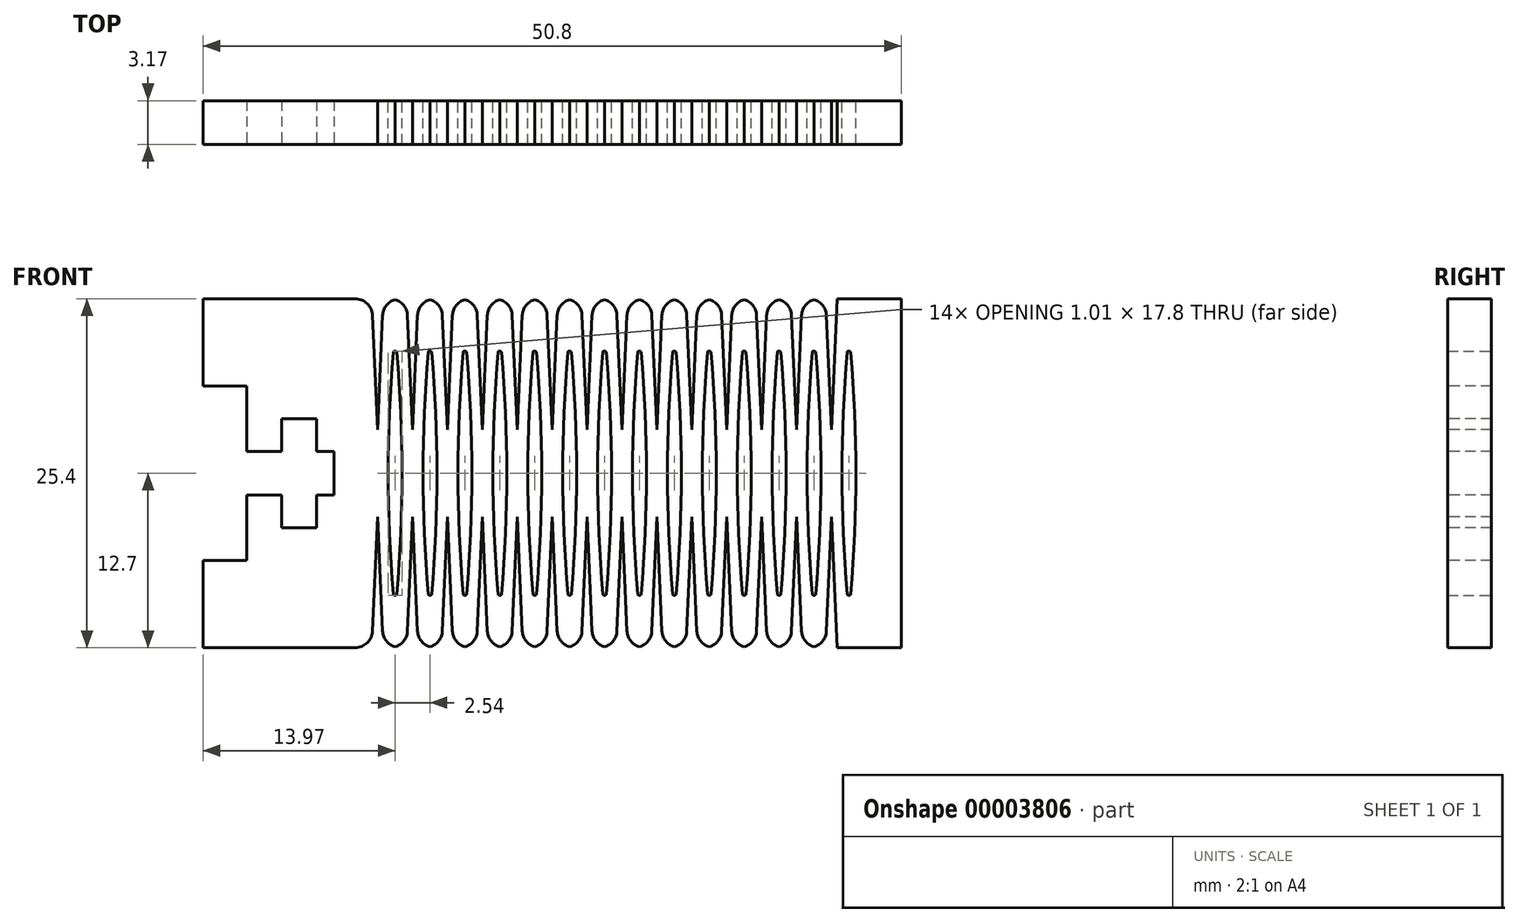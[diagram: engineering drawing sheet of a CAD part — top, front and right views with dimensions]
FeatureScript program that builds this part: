
annotation { "Feature Type Name" : "Feature", "Feature Type Description" : "" }
export const myFeature = defineFeature(function(context is Context, id is Id, definition is map)
    precondition{}
    {
        {
            var Q0;
            Q0=qCreatedBy(makeId("Front.planeOp"),FACE);
            var sketch = newSketch(context, id + "F0", { "sketchPlane" : qUnion([Q0])});
            skLineSegment(sketch, "E0.bottom", {"start": v(0, 0) * mm, "end": v(50.8, 0) * mm});
            skLineSegment(sketch, "E0.top", {"start": v(0, 25.4) * mm, "end": v(50.8, 25.4) * mm});
            skLineSegment(sketch, "E0.left", {"start": v(0, 0) * mm, "end": v(0, 25.4) * mm});
            skLineSegment(sketch, "E0.right", {"start": v(50.8, 0) * mm, "end": v(50.8, 25.4) * mm});
            skSolve(sketch);
        }
        {
            var Q0;
            Q0 = qSketchRegion(id + "F0", true);
            extrude(context, id + "F1", {"entities" : qUnion([Q0]), "oppositeDirection" : true, "depth" : 3.17 * mm});
        }
        {
            var Q0;
            Q0=makeQuery(id+"F1.opExtrude","CAP_FACE",FACE,{"disambiguationData":[OSD([sQuery(id+"F0.wireOp",EDGE,"E0.bottom"),sQuery(id+"F0.wireOp",EDGE,"E0.top"),sQuery(id+"F0.wireOp",EDGE,"E0.left"),sQuery(id+"F0.wireOp",EDGE,"E0.right")])],"isStart":true});
            var sketch = newSketch(context, id + "F2", { "sketchPlane" : qUnion([Q0])});
            skLineSegment(sketch, "E1.bottom", {"start": v(0, 6.35) * mm, "end": v(3.18, 6.35) * mm});
            skLineSegment(sketch, "E1.top", {"start": v(0, 19.05) * mm, "end": v(3.17, 19.05) * mm});
            skLineSegment(sketch, "E1.left", {"start": v(0, 6.35) * mm, "end": v(0, 19.05) * mm});
            skLineSegment(sketch, "E1.right", {"start": v(3.18, 6.35) * mm, "end": v(3.18, 19.05) * mm});
            skLineSegment(sketch, "E2.bottom", {"start": v(0, 11.11) * mm, "end": v(9.53, 11.11) * mm});
            skLineSegment(sketch, "E2.top", {"start": v(0, 14.29) * mm, "end": v(9.53, 14.29) * mm});
            skLineSegment(sketch, "E2.left", {"start": v(0, 11.11) * mm, "end": v(0, 14.29) * mm});
            skLineSegment(sketch, "E2.right", {"start": v(9.53, 11.11) * mm, "end": v(9.53, 14.29) * mm});
            skLineSegment(sketch, "E3.bottom", {"start": v(5.71, 16.67) * mm, "end": v(8.26, 16.67) * mm});
            skLineSegment(sketch, "E3.top", {"start": v(5.71, 8.73) * mm, "end": v(8.26, 8.73) * mm});
            skLineSegment(sketch, "E3.left", {"start": v(5.71, 16.67) * mm, "end": v(5.71, 8.73) * mm});
            skLineSegment(sketch, "E3.right", {"start": v(8.26, 16.67) * mm, "end": v(8.26, 8.73) * mm});
            skSolve(sketch);
        }
        {
            var Q0;
            Q0 = qSketchRegion(id + "F2", true);
            extrude(context, id + "F3", {"entities" : qUnion([Q0]), "operationType" : NewBodyOperationType.REMOVE, "endBound" : BoundingType.THROUGH_ALL, "oppositeDirection" : true, "depth" : 25.4 * mm});
        }
        {
            var Q0;
            Q0=makeQuery(id+"F1.opExtrude","CAP_FACE",FACE,{"disambiguationData":[OSD([sQuery(id+"F0.wireOp",EDGE,"E0.bottom"),sQuery(id+"F0.wireOp",EDGE,"E0.top"),sQuery(id+"F0.wireOp",EDGE,"E0.left"),sQuery(id+"F0.wireOp",EDGE,"E0.right")])],"isStart":true});
            var sketch = newSketch(context, id + "F4", { "sketchPlane" : qUnion([Q0])});
            skLineSegment(sketch, "E4", {"start": v(0, 9.53) * mm, "end": v(50.8, 9.53) * mm, "construction": true});
            skLineSegment(sketch, "E5", {"start": v(12.7, 9.53) * mm, "end": v(12.28, 0) * mm});
            skLineSegment(sketch, "E6", {"start": v(12.7, 9.53) * mm, "end": v(13.12, 0) * mm});
            skLineSegment(sketch, "E7", {"start": v(12.28, 0) * mm, "end": v(13.12, 0) * mm});
            skLineSegment(sketch, "E8", {"start": v(12.7, 0) * mm, "end": v(12.7, 9.53) * mm, "construction": true});
            skLineSegment(sketch, "E9", {"start": v(0, 12.7) * mm, "end": v(50.8, 12.7) * mm, "construction": true});
            skLineSegment(sketch, "E10.0.MirrorCS", {"start": v(12.7, 15.87) * mm, "end": v(13.12, 25.4) * mm});
            skLineSegment(sketch, "E11.0.MirrorCS", {"start": v(12.7, 15.88) * mm, "end": v(12.28, 25.4) * mm});
            skLineSegment(sketch, "E12.0.MirrorCS", {"start": v(12.28, 25.4) * mm, "end": v(13.12, 25.4) * mm});
            skLineSegment(sketch, "E13.1.0.0", {"start": v(15.24, 9.53) * mm, "end": v(15.66, 0) * mm});
            skLineSegment(sketch, "E13.1.0.1", {"start": v(15.24, 9.52) * mm, "end": v(14.82, 0) * mm});
            skLineSegment(sketch, "E13.1.0.2", {"start": v(14.82, 0) * mm, "end": v(15.66, 0) * mm});
            skLineSegment(sketch, "E13.2.0.0", {"start": v(17.78, 9.53) * mm, "end": v(18.2, 0) * mm});
            skLineSegment(sketch, "E13.2.0.1", {"start": v(17.78, 9.52) * mm, "end": v(17.36, 0) * mm});
            skLineSegment(sketch, "E13.2.0.2", {"start": v(17.36, 0) * mm, "end": v(18.2, 0) * mm});
            skLineSegment(sketch, "E13.3.0.0", {"start": v(20.32, 9.53) * mm, "end": v(20.74, 0) * mm});
            skLineSegment(sketch, "E13.3.0.1", {"start": v(20.32, 9.52) * mm, "end": v(19.9, 0) * mm});
            skLineSegment(sketch, "E13.3.0.2", {"start": v(19.9, 0) * mm, "end": v(20.74, 0) * mm});
            skLineSegment(sketch, "E13.4.0.0", {"start": v(22.86, 9.53) * mm, "end": v(23.28, 0) * mm});
            skLineSegment(sketch, "E13.4.0.1", {"start": v(22.86, 9.53) * mm, "end": v(22.44, 0) * mm});
            skLineSegment(sketch, "E13.4.0.2", {"start": v(22.44, 0) * mm, "end": v(23.28, 0) * mm});
            skLineSegment(sketch, "E13.5.0.0", {"start": v(25.4, 9.53) * mm, "end": v(25.82, 0) * mm});
            skLineSegment(sketch, "E13.5.0.1", {"start": v(25.4, 9.52) * mm, "end": v(24.98, 0) * mm});
            skLineSegment(sketch, "E13.5.0.2", {"start": v(24.98, 0) * mm, "end": v(25.82, 0) * mm});
            skLineSegment(sketch, "E13.6.0.0", {"start": v(27.94, 9.53) * mm, "end": v(28.36, 0) * mm});
            skLineSegment(sketch, "E13.6.0.1", {"start": v(27.94, 9.52) * mm, "end": v(27.52, 0) * mm});
            skLineSegment(sketch, "E13.6.0.2", {"start": v(27.52, 0) * mm, "end": v(28.36, 0) * mm});
            skLineSegment(sketch, "E13.7.0.0", {"start": v(30.48, 9.53) * mm, "end": v(30.9, 0) * mm});
            skLineSegment(sketch, "E13.7.0.1", {"start": v(30.48, 9.52) * mm, "end": v(30.06, 0) * mm});
            skLineSegment(sketch, "E13.7.0.2", {"start": v(30.06, 0) * mm, "end": v(30.9, 0) * mm});
            skLineSegment(sketch, "E13.8.0.0", {"start": v(33.02, 9.53) * mm, "end": v(33.44, 0) * mm});
            skLineSegment(sketch, "E13.8.0.1", {"start": v(33.02, 9.52) * mm, "end": v(32.6, 0) * mm});
            skLineSegment(sketch, "E13.8.0.2", {"start": v(32.6, 0) * mm, "end": v(33.44, 0) * mm});
            skLineSegment(sketch, "E13.9.0.0", {"start": v(35.56, 9.53) * mm, "end": v(35.98, 0) * mm});
            skLineSegment(sketch, "E13.9.0.1", {"start": v(35.56, 9.53) * mm, "end": v(35.14, 0) * mm});
            skLineSegment(sketch, "E13.9.0.2", {"start": v(35.14, 0) * mm, "end": v(35.98, 0) * mm});
            skLineSegment(sketch, "E13.10.0.0", {"start": v(38.1, 9.53) * mm, "end": v(38.52, 0) * mm});
            skLineSegment(sketch, "E13.10.0.1", {"start": v(38.1, 9.53) * mm, "end": v(37.68, 0) * mm});
            skLineSegment(sketch, "E13.10.0.2", {"start": v(37.68, 0) * mm, "end": v(38.52, 0) * mm});
            skLineSegment(sketch, "E13.11.0.0", {"start": v(40.64, 9.53) * mm, "end": v(41.06, 0) * mm});
            skLineSegment(sketch, "E13.11.0.1", {"start": v(40.64, 9.52) * mm, "end": v(40.22, 0) * mm});
            skLineSegment(sketch, "E13.11.0.2", {"start": v(40.22, 0) * mm, "end": v(41.06, 0) * mm});
            skLineSegment(sketch, "E13.12.0.0", {"start": v(43.18, 9.53) * mm, "end": v(43.6, 0) * mm});
            skLineSegment(sketch, "E13.12.0.1", {"start": v(43.18, 9.52) * mm, "end": v(42.76, 0) * mm});
            skLineSegment(sketch, "E13.12.0.2", {"start": v(42.76, 0) * mm, "end": v(43.6, 0) * mm});
            skLineSegment(sketch, "E13.13.0.0", {"start": v(45.72, 9.53) * mm, "end": v(46.14, 0) * mm});
            skLineSegment(sketch, "E13.13.0.1", {"start": v(45.72, 9.52) * mm, "end": v(45.3, 0) * mm});
            skLineSegment(sketch, "E13.13.0.2", {"start": v(45.3, 0) * mm, "end": v(46.14, 0) * mm});
            skLineSegment(sketch, "E13.direction1", {"start": v(13.12, 0) * mm, "end": v(15.66, 0) * mm, "construction": true});
            skLineSegment(sketch, "E14.1.MirrorCS", {"start": v(30.06, 25.4) * mm, "end": v(30.9, 25.4) * mm});
            skLineSegment(sketch, "E14.2.MirrorCS", {"start": v(14.82, 25.4) * mm, "end": v(15.66, 25.4) * mm});
            skLineSegment(sketch, "E14.4.MirrorCS", {"start": v(22.44, 25.4) * mm, "end": v(23.28, 25.4) * mm});
            skLineSegment(sketch, "E14.5.MirrorCS", {"start": v(42.76, 25.4) * mm, "end": v(43.6, 25.4) * mm});
            skLineSegment(sketch, "E14.6.MirrorCS", {"start": v(40.22, 25.4) * mm, "end": v(41.06, 25.4) * mm});
            skLineSegment(sketch, "E14.8.MirrorCS", {"start": v(27.52, 25.4) * mm, "end": v(28.36, 25.4) * mm});
            skLineSegment(sketch, "E14.9.MirrorCS", {"start": v(35.14, 25.4) * mm, "end": v(35.98, 25.4) * mm});
            skLineSegment(sketch, "E14.10.MirrorCS", {"start": v(32.6, 25.4) * mm, "end": v(33.44, 25.4) * mm});
            skLineSegment(sketch, "E14.11.MirrorCS", {"start": v(24.98, 25.4) * mm, "end": v(25.82, 25.4) * mm});
            skLineSegment(sketch, "E14.13.MirrorCS", {"start": v(19.9, 25.4) * mm, "end": v(20.74, 25.4) * mm});
            skLineSegment(sketch, "E14.14.MirrorCS", {"start": v(37.68, 25.4) * mm, "end": v(38.52, 25.4) * mm});
            skLineSegment(sketch, "E14.15.MirrorCS", {"start": v(45.3, 25.4) * mm, "end": v(46.14, 25.4) * mm});
            skLineSegment(sketch, "E14.16.MirrorCS", {"start": v(17.36, 25.4) * mm, "end": v(18.2, 25.4) * mm});
            skLineSegment(sketch, "E14.17.MirrorCS", {"start": v(43.18, 15.88) * mm, "end": v(42.76, 25.4) * mm});
            skLineSegment(sketch, "E14.18.MirrorCS", {"start": v(30.48, 15.88) * mm, "end": v(30.9, 25.4) * mm});
            skLineSegment(sketch, "E14.19.MirrorCS", {"start": v(38.1, 15.88) * mm, "end": v(38.52, 25.4) * mm});
            skLineSegment(sketch, "E14.21.MirrorCS", {"start": v(30.48, 15.88) * mm, "end": v(30.06, 25.4) * mm});
            skLineSegment(sketch, "E14.22.MirrorCS", {"start": v(38.1, 15.88) * mm, "end": v(37.68, 25.4) * mm});
            skLineSegment(sketch, "E14.23.MirrorCS", {"start": v(25.4, 15.88) * mm, "end": v(25.82, 25.4) * mm});
            skLineSegment(sketch, "E14.24.MirrorCS", {"start": v(27.94, 15.88) * mm, "end": v(27.52, 25.4) * mm});
            skLineSegment(sketch, "E14.26.MirrorCS", {"start": v(35.56, 15.88) * mm, "end": v(35.14, 25.4) * mm});
            skLineSegment(sketch, "E14.27.MirrorCS", {"start": v(22.86, 15.88) * mm, "end": v(23.28, 25.4) * mm});
            skLineSegment(sketch, "E14.28.MirrorCS", {"start": v(43.18, 15.88) * mm, "end": v(43.6, 25.4) * mm});
            skLineSegment(sketch, "E14.30.MirrorCS", {"start": v(22.86, 15.88) * mm, "end": v(22.44, 25.4) * mm});
            skLineSegment(sketch, "E14.33.MirrorCS", {"start": v(20.32, 15.88) * mm, "end": v(19.9, 25.4) * mm});
            skLineSegment(sketch, "E14.34.MirrorCS", {"start": v(40.64, 15.88) * mm, "end": v(41.06, 25.4) * mm});
            skLineSegment(sketch, "E14.36.MirrorCS", {"start": v(27.94, 15.88) * mm, "end": v(28.36, 25.4) * mm});
            skLineSegment(sketch, "E14.37.MirrorCS", {"start": v(40.64, 15.88) * mm, "end": v(40.22, 25.4) * mm});
            skLineSegment(sketch, "E14.39.MirrorCS", {"start": v(35.56, 15.88) * mm, "end": v(35.98, 25.4) * mm});
            skLineSegment(sketch, "E14.41.MirrorCS", {"start": v(25.4, 15.88) * mm, "end": v(24.98, 25.4) * mm});
            skLineSegment(sketch, "E14.42.MirrorCS", {"start": v(33.02, 15.88) * mm, "end": v(32.6, 25.4) * mm});
            skLineSegment(sketch, "E14.43.MirrorCS", {"start": v(17.78, 15.88) * mm, "end": v(17.36, 25.4) * mm});
            skLineSegment(sketch, "E14.44.MirrorCS", {"start": v(45.72, 15.88) * mm, "end": v(46.14, 25.4) * mm});
            skLineSegment(sketch, "E14.45.MirrorCS", {"start": v(20.32, 15.88) * mm, "end": v(20.74, 25.4) * mm});
            skLineSegment(sketch, "E14.46.MirrorCS", {"start": v(45.72, 15.88) * mm, "end": v(45.3, 25.4) * mm});
            skLineSegment(sketch, "E14.47.MirrorCS", {"start": v(15.24, 15.88) * mm, "end": v(15.66, 25.4) * mm});
            skLineSegment(sketch, "E14.48.MirrorCS", {"start": v(33.02, 15.88) * mm, "end": v(33.44, 25.4) * mm});
            skLineSegment(sketch, "E14.49.MirrorCS", {"start": v(15.24, 15.88) * mm, "end": v(14.82, 25.4) * mm});
            skLineSegment(sketch, "E14.50.MirrorCS", {"start": v(17.78, 15.88) * mm, "end": v(18.2, 25.4) * mm});
            skLineSegment(sketch, "E15", {"start": v(13.97, 22.86) * mm, "end": v(13.97, 2.54) * mm, "construction": true});
            skLineSegment(sketch, "E16", {"start": v(13.02, 12.7) * mm, "end": v(14.92, 12.7) * mm, "construction": true});
            skLineSegment(sketch, "E17", {"start": v(13.97, 22.86) * mm, "end": v(13.02, 12.7) * mm});
            skLineSegment(sketch, "E18", {"start": v(13.97, 2.54) * mm, "end": v(14.92, 12.7) * mm});
            skLineSegment(sketch, "E19", {"start": v(14.92, 12.7) * mm, "end": v(13.97, 22.86) * mm});
            skLineSegment(sketch, "E20", {"start": v(13.02, 12.7) * mm, "end": v(13.97, 2.54) * mm});
            skLineSegment(sketch, "E21.1.0.0", {"start": v(16.51, 22.86) * mm, "end": v(15.56, 12.7) * mm});
            skLineSegment(sketch, "E21.1.0.1", {"start": v(17.46, 12.7) * mm, "end": v(16.51, 22.86) * mm});
            skLineSegment(sketch, "E21.1.0.2", {"start": v(15.56, 12.7) * mm, "end": v(16.51, 2.54) * mm});
            skLineSegment(sketch, "E21.1.0.3", {"start": v(16.51, 2.54) * mm, "end": v(17.46, 12.7) * mm});
            skLineSegment(sketch, "E21.2.0.0", {"start": v(19.05, 22.86) * mm, "end": v(18.1, 12.7) * mm});
            skLineSegment(sketch, "E21.2.0.1", {"start": v(20, 12.7) * mm, "end": v(19.05, 22.86) * mm});
            skLineSegment(sketch, "E21.2.0.2", {"start": v(18.1, 12.7) * mm, "end": v(19.05, 2.54) * mm});
            skLineSegment(sketch, "E21.2.0.3", {"start": v(19.05, 2.54) * mm, "end": v(20, 12.7) * mm});
            skLineSegment(sketch, "E21.3.0.0", {"start": v(21.6, 22.86) * mm, "end": v(20.64, 12.7) * mm});
            skLineSegment(sketch, "E21.3.0.1", {"start": v(22.54, 12.7) * mm, "end": v(21.59, 22.86) * mm});
            skLineSegment(sketch, "E21.3.0.2", {"start": v(20.64, 12.7) * mm, "end": v(21.6, 2.54) * mm});
            skLineSegment(sketch, "E21.3.0.3", {"start": v(21.6, 2.54) * mm, "end": v(22.54, 12.7) * mm});
            skLineSegment(sketch, "E21.4.0.0", {"start": v(24.13, 22.86) * mm, "end": v(23.18, 12.7) * mm});
            skLineSegment(sketch, "E21.4.0.1", {"start": v(25.08, 12.7) * mm, "end": v(24.13, 22.86) * mm});
            skLineSegment(sketch, "E21.4.0.2", {"start": v(23.18, 12.7) * mm, "end": v(24.13, 2.54) * mm});
            skLineSegment(sketch, "E21.4.0.3", {"start": v(24.13, 2.54) * mm, "end": v(25.08, 12.7) * mm});
            skLineSegment(sketch, "E21.5.0.0", {"start": v(26.67, 22.86) * mm, "end": v(25.72, 12.7) * mm});
            skLineSegment(sketch, "E21.5.0.1", {"start": v(27.62, 12.7) * mm, "end": v(26.67, 22.86) * mm});
            skLineSegment(sketch, "E21.5.0.2", {"start": v(25.72, 12.7) * mm, "end": v(26.67, 2.54) * mm});
            skLineSegment(sketch, "E21.5.0.3", {"start": v(26.67, 2.54) * mm, "end": v(27.62, 12.7) * mm});
            skLineSegment(sketch, "E21.6.0.0", {"start": v(29.21, 22.86) * mm, "end": v(28.26, 12.7) * mm});
            skLineSegment(sketch, "E21.6.0.1", {"start": v(30.16, 12.7) * mm, "end": v(29.21, 22.86) * mm});
            skLineSegment(sketch, "E21.6.0.2", {"start": v(28.26, 12.7) * mm, "end": v(29.21, 2.54) * mm});
            skLineSegment(sketch, "E21.6.0.3", {"start": v(29.21, 2.54) * mm, "end": v(30.16, 12.7) * mm});
            skLineSegment(sketch, "E21.7.0.0", {"start": v(31.75, 22.86) * mm, "end": v(30.8, 12.7) * mm});
            skLineSegment(sketch, "E21.7.0.1", {"start": v(32.7, 12.7) * mm, "end": v(31.75, 22.86) * mm});
            skLineSegment(sketch, "E21.7.0.2", {"start": v(30.8, 12.7) * mm, "end": v(31.75, 2.54) * mm});
            skLineSegment(sketch, "E21.7.0.3", {"start": v(31.75, 2.54) * mm, "end": v(32.7, 12.7) * mm});
            skLineSegment(sketch, "E21.8.0.0", {"start": v(34.3, 22.86) * mm, "end": v(33.34, 12.7) * mm});
            skLineSegment(sketch, "E21.8.0.1", {"start": v(35.24, 12.7) * mm, "end": v(34.3, 22.86) * mm});
            skLineSegment(sketch, "E21.8.0.2", {"start": v(33.34, 12.7) * mm, "end": v(34.3, 2.54) * mm});
            skLineSegment(sketch, "E21.8.0.3", {"start": v(34.3, 2.54) * mm, "end": v(35.24, 12.7) * mm});
            skLineSegment(sketch, "E21.9.0.0", {"start": v(36.83, 22.86) * mm, "end": v(35.88, 12.7) * mm});
            skLineSegment(sketch, "E21.9.0.1", {"start": v(37.78, 12.7) * mm, "end": v(36.83, 22.86) * mm});
            skLineSegment(sketch, "E21.9.0.2", {"start": v(35.88, 12.7) * mm, "end": v(36.83, 2.54) * mm});
            skLineSegment(sketch, "E21.9.0.3", {"start": v(36.83, 2.54) * mm, "end": v(37.78, 12.7) * mm});
            skLineSegment(sketch, "E21.10.0.0", {"start": v(39.37, 22.86) * mm, "end": v(38.42, 12.7) * mm});
            skLineSegment(sketch, "E21.10.0.1", {"start": v(40.32, 12.7) * mm, "end": v(39.37, 22.86) * mm});
            skLineSegment(sketch, "E21.10.0.2", {"start": v(38.42, 12.7) * mm, "end": v(39.37, 2.54) * mm});
            skLineSegment(sketch, "E21.10.0.3", {"start": v(39.37, 2.54) * mm, "end": v(40.32, 12.7) * mm});
            skLineSegment(sketch, "E21.11.0.0", {"start": v(41.91, 22.86) * mm, "end": v(40.96, 12.7) * mm});
            skLineSegment(sketch, "E21.11.0.1", {"start": v(42.86, 12.7) * mm, "end": v(41.91, 22.86) * mm});
            skLineSegment(sketch, "E21.11.0.2", {"start": v(40.96, 12.7) * mm, "end": v(41.91, 2.54) * mm});
            skLineSegment(sketch, "E21.11.0.3", {"start": v(41.91, 2.54) * mm, "end": v(42.86, 12.7) * mm});
            skLineSegment(sketch, "E21.12.0.0", {"start": v(44.45, 22.86) * mm, "end": v(43.5, 12.7) * mm});
            skLineSegment(sketch, "E21.12.0.1", {"start": v(45.4, 12.7) * mm, "end": v(44.45, 22.86) * mm});
            skLineSegment(sketch, "E21.12.0.2", {"start": v(43.5, 12.7) * mm, "end": v(44.45, 2.54) * mm});
            skLineSegment(sketch, "E21.12.0.3", {"start": v(44.45, 2.54) * mm, "end": v(45.4, 12.7) * mm});
            skLineSegment(sketch, "E21.13.0.0", {"start": v(47, 22.86) * mm, "end": v(46.04, 12.7) * mm});
            skLineSegment(sketch, "E21.13.0.1", {"start": v(47.94, 12.7) * mm, "end": v(47, 22.86) * mm});
            skLineSegment(sketch, "E21.13.0.2", {"start": v(46.04, 12.7) * mm, "end": v(47, 2.54) * mm});
            skLineSegment(sketch, "E21.13.0.3", {"start": v(47, 2.54) * mm, "end": v(47.94, 12.7) * mm});
            skLineSegment(sketch, "E21.direction1", {"start": v(13.02, 12.7) * mm, "end": v(15.56, 12.7) * mm, "construction": true});
            skSolve(sketch);
        }
        {
            var Q0;
            Q0 = qSketchRegion(id + "F4", true);
            extrude(context, id + "F5", {"entities" : qUnion([Q0]), "operationType" : NewBodyOperationType.REMOVE, "endBound" : BoundingType.THROUGH_ALL, "oppositeDirection" : true, "depth" : 25.4 * mm});
        }
        {
            var Q0;
            Q0=makeQuery(id+"F5.boolean.opBoolean","COPY",EDGE,{"derivedFrom":makeQuery(id+"F5.opExtrude","SWEPT_EDGE",EDGE,{"disambiguationData":[OSD([sQuery(id+"F4.wireOp",EDGE,"E17"),sQuery(id+"F4.wireOp",EDGE,"E20")])]})});
            var Q1;
            Q1=makeQuery(id+"F5.boolean.opBoolean","COPY",EDGE,{"derivedFrom":makeQuery(id+"F5.opExtrude","SWEPT_EDGE",EDGE,{"disambiguationData":[OSD([sQuery(id+"F4.wireOp",EDGE,"E21.1.0.0"),sQuery(id+"F4.wireOp",EDGE,"E21.1.0.2")])]})});
            var Q2;
            Q2=makeQuery(id+"F5.boolean.opBoolean","COPY",EDGE,{"derivedFrom":makeQuery(id+"F5.opExtrude","SWEPT_EDGE",EDGE,{"disambiguationData":[OSD([sQuery(id+"F4.wireOp",EDGE,"E21.2.0.0"),sQuery(id+"F4.wireOp",EDGE,"E21.2.0.2")])]})});
            var Q3;
            Q3=makeQuery(id+"F5.boolean.opBoolean","COPY",EDGE,{"derivedFrom":makeQuery(id+"F5.opExtrude","SWEPT_EDGE",EDGE,{"disambiguationData":[OSD([sQuery(id+"F4.wireOp",EDGE,"E21.3.0.0"),sQuery(id+"F4.wireOp",EDGE,"E21.3.0.2")])]})});
            var Q4;
            Q4=makeQuery(id+"F5.boolean.opBoolean","COPY",EDGE,{"derivedFrom":makeQuery(id+"F5.opExtrude","SWEPT_EDGE",EDGE,{"disambiguationData":[OSD([sQuery(id+"F4.wireOp",EDGE,"E21.4.0.0"),sQuery(id+"F4.wireOp",EDGE,"E21.4.0.2")])]})});
            var Q5;
            Q5=makeQuery(id+"F5.boolean.opBoolean","COPY",EDGE,{"derivedFrom":makeQuery(id+"F5.opExtrude","SWEPT_EDGE",EDGE,{"disambiguationData":[OSD([sQuery(id+"F4.wireOp",EDGE,"E21.5.0.0"),sQuery(id+"F4.wireOp",EDGE,"E21.5.0.2")])]})});
            var Q6;
            Q6=makeQuery(id+"F5.boolean.opBoolean","COPY",EDGE,{"derivedFrom":makeQuery(id+"F5.opExtrude","SWEPT_EDGE",EDGE,{"disambiguationData":[OSD([sQuery(id+"F4.wireOp",EDGE,"E21.6.0.0"),sQuery(id+"F4.wireOp",EDGE,"E21.6.0.2")])]})});
            var Q7;
            Q7=makeQuery(id+"F5.boolean.opBoolean","COPY",EDGE,{"derivedFrom":makeQuery(id+"F5.opExtrude","SWEPT_EDGE",EDGE,{"disambiguationData":[OSD([sQuery(id+"F4.wireOp",EDGE,"E21.7.0.0"),sQuery(id+"F4.wireOp",EDGE,"E21.7.0.2")])]})});
            var Q8;
            Q8=makeQuery(id+"F5.boolean.opBoolean","COPY",EDGE,{"derivedFrom":makeQuery(id+"F5.opExtrude","SWEPT_EDGE",EDGE,{"disambiguationData":[OSD([sQuery(id+"F4.wireOp",EDGE,"E21.8.0.0"),sQuery(id+"F4.wireOp",EDGE,"E21.8.0.2")])]})});
            var Q9;
            Q9=makeQuery(id+"F5.boolean.opBoolean","COPY",EDGE,{"derivedFrom":makeQuery(id+"F5.opExtrude","SWEPT_EDGE",EDGE,{"disambiguationData":[OSD([sQuery(id+"F4.wireOp",EDGE,"E21.9.0.0"),sQuery(id+"F4.wireOp",EDGE,"E21.9.0.2")])]})});
            var Q10;
            Q10=makeQuery(id+"F5.boolean.opBoolean","COPY",EDGE,{"derivedFrom":makeQuery(id+"F5.opExtrude","SWEPT_EDGE",EDGE,{"disambiguationData":[OSD([sQuery(id+"F4.wireOp",EDGE,"E21.10.0.0"),sQuery(id+"F4.wireOp",EDGE,"E21.10.0.2")])]})});
            var Q11;
            Q11=makeQuery(id+"F5.boolean.opBoolean","COPY",EDGE,{"derivedFrom":makeQuery(id+"F5.opExtrude","SWEPT_EDGE",EDGE,{"disambiguationData":[OSD([sQuery(id+"F4.wireOp",EDGE,"E21.11.0.0"),sQuery(id+"F4.wireOp",EDGE,"E21.11.0.2")])]})});
            var Q12;
            Q12=makeQuery(id+"F5.boolean.opBoolean","COPY",EDGE,{"derivedFrom":makeQuery(id+"F5.opExtrude","SWEPT_EDGE",EDGE,{"disambiguationData":[OSD([sQuery(id+"F4.wireOp",EDGE,"E21.12.0.0"),sQuery(id+"F4.wireOp",EDGE,"E21.12.0.2")])]})});
            var Q13;
            Q13=makeQuery(id+"F5.boolean.opBoolean","COPY",EDGE,{"derivedFrom":makeQuery(id+"F5.opExtrude","SWEPT_EDGE",EDGE,{"disambiguationData":[OSD([sQuery(id+"F4.wireOp",EDGE,"E21.13.0.0"),sQuery(id+"F4.wireOp",EDGE,"E21.13.0.2")])]})});
            var Q14;
            Q14=makeQuery(id+"F5.boolean.opBoolean","COPY",EDGE,{"derivedFrom":makeQuery(id+"F5.opExtrude","SWEPT_EDGE",EDGE,{"disambiguationData":[OSD([sQuery(id+"F4.wireOp",EDGE,"E21.13.0.1"),sQuery(id+"F4.wireOp",EDGE,"E21.13.0.3")])]})});
            var Q15;
            Q15=makeQuery(id+"F5.boolean.opBoolean","COPY",EDGE,{"derivedFrom":makeQuery(id+"F5.opExtrude","SWEPT_EDGE",EDGE,{"disambiguationData":[OSD([sQuery(id+"F4.wireOp",EDGE,"E21.12.0.1"),sQuery(id+"F4.wireOp",EDGE,"E21.12.0.3")])]})});
            var Q16;
            Q16=makeQuery(id+"F5.boolean.opBoolean","COPY",EDGE,{"derivedFrom":makeQuery(id+"F5.opExtrude","SWEPT_EDGE",EDGE,{"disambiguationData":[OSD([sQuery(id+"F4.wireOp",EDGE,"E21.11.0.1"),sQuery(id+"F4.wireOp",EDGE,"E21.11.0.3")])]})});
            var Q17;
            Q17=makeQuery(id+"F5.boolean.opBoolean","COPY",EDGE,{"derivedFrom":makeQuery(id+"F5.opExtrude","SWEPT_EDGE",EDGE,{"disambiguationData":[OSD([sQuery(id+"F4.wireOp",EDGE,"E21.10.0.1"),sQuery(id+"F4.wireOp",EDGE,"E21.10.0.3")])]})});
            var Q18;
            Q18=makeQuery(id+"F5.boolean.opBoolean","COPY",EDGE,{"derivedFrom":makeQuery(id+"F5.opExtrude","SWEPT_EDGE",EDGE,{"disambiguationData":[OSD([sQuery(id+"F4.wireOp",EDGE,"E21.9.0.1"),sQuery(id+"F4.wireOp",EDGE,"E21.9.0.3")])]})});
            var Q19;
            Q19=makeQuery(id+"F5.boolean.opBoolean","COPY",EDGE,{"derivedFrom":makeQuery(id+"F5.opExtrude","SWEPT_EDGE",EDGE,{"disambiguationData":[OSD([sQuery(id+"F4.wireOp",EDGE,"E21.8.0.1"),sQuery(id+"F4.wireOp",EDGE,"E21.8.0.3")])]})});
            var Q20;
            Q20=makeQuery(id+"F5.boolean.opBoolean","COPY",EDGE,{"derivedFrom":makeQuery(id+"F5.opExtrude","SWEPT_EDGE",EDGE,{"disambiguationData":[OSD([sQuery(id+"F4.wireOp",EDGE,"E21.7.0.1"),sQuery(id+"F4.wireOp",EDGE,"E21.7.0.3")])]})});
            var Q21;
            Q21=makeQuery(id+"F5.boolean.opBoolean","COPY",EDGE,{"derivedFrom":makeQuery(id+"F5.opExtrude","SWEPT_EDGE",EDGE,{"disambiguationData":[OSD([sQuery(id+"F4.wireOp",EDGE,"E21.6.0.1"),sQuery(id+"F4.wireOp",EDGE,"E21.6.0.3")])]})});
            var Q22;
            Q22=makeQuery(id+"F5.boolean.opBoolean","COPY",EDGE,{"derivedFrom":makeQuery(id+"F5.opExtrude","SWEPT_EDGE",EDGE,{"disambiguationData":[OSD([sQuery(id+"F4.wireOp",EDGE,"E21.5.0.1"),sQuery(id+"F4.wireOp",EDGE,"E21.5.0.3")])]})});
            var Q23;
            Q23=makeQuery(id+"F5.boolean.opBoolean","COPY",EDGE,{"derivedFrom":makeQuery(id+"F5.opExtrude","SWEPT_EDGE",EDGE,{"disambiguationData":[OSD([sQuery(id+"F4.wireOp",EDGE,"E21.4.0.1"),sQuery(id+"F4.wireOp",EDGE,"E21.4.0.3")])]})});
            var Q24;
            Q24=makeQuery(id+"F5.boolean.opBoolean","COPY",EDGE,{"derivedFrom":makeQuery(id+"F5.opExtrude","SWEPT_EDGE",EDGE,{"disambiguationData":[OSD([sQuery(id+"F4.wireOp",EDGE,"E21.3.0.1"),sQuery(id+"F4.wireOp",EDGE,"E21.3.0.3")])]})});
            var Q25;
            Q25=makeQuery(id+"F5.boolean.opBoolean","COPY",EDGE,{"derivedFrom":makeQuery(id+"F5.opExtrude","SWEPT_EDGE",EDGE,{"disambiguationData":[OSD([sQuery(id+"F4.wireOp",EDGE,"E21.2.0.1"),sQuery(id+"F4.wireOp",EDGE,"E21.2.0.3")])]})});
            var Q26;
            Q26=makeQuery(id+"F5.boolean.opBoolean","COPY",EDGE,{"derivedFrom":makeQuery(id+"F5.opExtrude","SWEPT_EDGE",EDGE,{"disambiguationData":[OSD([sQuery(id+"F4.wireOp",EDGE,"E21.1.0.1"),sQuery(id+"F4.wireOp",EDGE,"E21.1.0.3")])]})});
            var Q27;
            Q27=makeQuery(id+"F5.boolean.opBoolean","COPY",EDGE,{"derivedFrom":makeQuery(id+"F5.opExtrude","SWEPT_EDGE",EDGE,{"disambiguationData":[OSD([sQuery(id+"F4.wireOp",EDGE,"E18"),sQuery(id+"F4.wireOp",EDGE,"E19")])]})});
            fillet(context, id + "F6", {"entities" : qUnion([Q0, Q1, Q2, Q3, Q4, Q5, Q6, Q7, Q8, Q9, Q10, Q11, Q12, Q13, Q14, Q15, Q16, Q17, Q18, Q19, Q20, Q21, Q22, Q23, Q24, Q25, Q26, Q27]), "radius" : 101.6 * mm, "tangentPropagation" : true, "allowEdgeOverflow" : false});
        }
        {
            var Q0;
            Q0=makeQuery(id+"F5.boolean.opBoolean","COPY",EDGE,{"derivedFrom":makeQuery(id+"F5.opExtrude","SWEPT_EDGE",EDGE,{"disambiguationData":[OSD([sQuery(id+"F0.wireOp",EDGE,"E0.top"),sQuery(id+"F4.wireOp",EDGE,"E11.0.MirrorCS"),sQuery(id+"F4.wireOp",EDGE,"E12.0.MirrorCS")])]})});
            var Q1;
            Q1=makeQuery(id+"F5.boolean.opBoolean","COPY",EDGE,{"derivedFrom":makeQuery(id+"F5.opExtrude","SWEPT_EDGE",EDGE,{"disambiguationData":[OSD([sQuery(id+"F0.wireOp",EDGE,"E0.top"),sQuery(id+"F4.wireOp",EDGE,"E10.0.MirrorCS"),sQuery(id+"F4.wireOp",EDGE,"E12.0.MirrorCS")])]})});
            var Q2;
            Q2=makeQuery(id+"F5.boolean.opBoolean","COPY",EDGE,{"derivedFrom":makeQuery(id+"F5.opExtrude","SWEPT_EDGE",EDGE,{"disambiguationData":[OSD([sQuery(id+"F0.wireOp",EDGE,"E0.top"),sQuery(id+"F4.wireOp",EDGE,"E14.49.MirrorCS"),sQuery(id+"F4.wireOp",EDGE,"E14.2.MirrorCS")])]})});
            var Q3;
            Q3=makeQuery(id+"F5.boolean.opBoolean","COPY",EDGE,{"derivedFrom":makeQuery(id+"F5.opExtrude","SWEPT_EDGE",EDGE,{"disambiguationData":[OSD([sQuery(id+"F0.wireOp",EDGE,"E0.top"),sQuery(id+"F4.wireOp",EDGE,"E14.2.MirrorCS"),sQuery(id+"F4.wireOp",EDGE,"E14.47.MirrorCS")])]})});
            var Q4;
            Q4=makeQuery(id+"F5.boolean.opBoolean","COPY",EDGE,{"derivedFrom":makeQuery(id+"F5.opExtrude","SWEPT_EDGE",EDGE,{"disambiguationData":[OSD([sQuery(id+"F0.wireOp",EDGE,"E0.top"),sQuery(id+"F4.wireOp",EDGE,"E14.43.MirrorCS"),sQuery(id+"F4.wireOp",EDGE,"E14.16.MirrorCS")])]})});
            var Q5;
            Q5=makeQuery(id+"F5.boolean.opBoolean","COPY",EDGE,{"derivedFrom":makeQuery(id+"F5.opExtrude","SWEPT_EDGE",EDGE,{"disambiguationData":[OSD([sQuery(id+"F0.wireOp",EDGE,"E0.top"),sQuery(id+"F4.wireOp",EDGE,"E14.16.MirrorCS"),sQuery(id+"F4.wireOp",EDGE,"E14.50.MirrorCS")])]})});
            var Q6;
            Q6=makeQuery(id+"F5.boolean.opBoolean","COPY",EDGE,{"derivedFrom":makeQuery(id+"F5.opExtrude","SWEPT_EDGE",EDGE,{"disambiguationData":[OSD([sQuery(id+"F0.wireOp",EDGE,"E0.top"),sQuery(id+"F4.wireOp",EDGE,"E14.33.MirrorCS"),sQuery(id+"F4.wireOp",EDGE,"E14.13.MirrorCS")])]})});
            var Q7;
            Q7=makeQuery(id+"F5.boolean.opBoolean","COPY",EDGE,{"derivedFrom":makeQuery(id+"F5.opExtrude","SWEPT_EDGE",EDGE,{"disambiguationData":[OSD([sQuery(id+"F0.wireOp",EDGE,"E0.top"),sQuery(id+"F4.wireOp",EDGE,"E14.13.MirrorCS"),sQuery(id+"F4.wireOp",EDGE,"E14.45.MirrorCS")])]})});
            var Q8;
            Q8=makeQuery(id+"F5.boolean.opBoolean","COPY",EDGE,{"derivedFrom":makeQuery(id+"F5.opExtrude","SWEPT_EDGE",EDGE,{"disambiguationData":[OSD([sQuery(id+"F0.wireOp",EDGE,"E0.top"),sQuery(id+"F4.wireOp",EDGE,"E14.4.MirrorCS"),sQuery(id+"F4.wireOp",EDGE,"E14.30.MirrorCS")])]})});
            var Q9;
            Q9=makeQuery(id+"F5.boolean.opBoolean","COPY",EDGE,{"derivedFrom":makeQuery(id+"F5.opExtrude","SWEPT_EDGE",EDGE,{"disambiguationData":[OSD([sQuery(id+"F0.wireOp",EDGE,"E0.top"),sQuery(id+"F4.wireOp",EDGE,"E14.4.MirrorCS"),sQuery(id+"F4.wireOp",EDGE,"E14.27.MirrorCS")])]})});
            var Q10;
            Q10=makeQuery(id+"F5.boolean.opBoolean","COPY",EDGE,{"derivedFrom":makeQuery(id+"F5.opExtrude","SWEPT_EDGE",EDGE,{"disambiguationData":[OSD([sQuery(id+"F0.wireOp",EDGE,"E0.top"),sQuery(id+"F4.wireOp",EDGE,"E14.11.MirrorCS"),sQuery(id+"F4.wireOp",EDGE,"E14.41.MirrorCS")])]})});
            var Q11;
            Q11=makeQuery(id+"F5.boolean.opBoolean","COPY",EDGE,{"derivedFrom":makeQuery(id+"F5.opExtrude","SWEPT_EDGE",EDGE,{"disambiguationData":[OSD([sQuery(id+"F0.wireOp",EDGE,"E0.top"),sQuery(id+"F4.wireOp",EDGE,"E14.11.MirrorCS"),sQuery(id+"F4.wireOp",EDGE,"E14.23.MirrorCS")])]})});
            var Q12;
            Q12=makeQuery(id+"F5.boolean.opBoolean","COPY",EDGE,{"derivedFrom":makeQuery(id+"F5.opExtrude","SWEPT_EDGE",EDGE,{"disambiguationData":[OSD([sQuery(id+"F0.wireOp",EDGE,"E0.top"),sQuery(id+"F4.wireOp",EDGE,"E14.8.MirrorCS"),sQuery(id+"F4.wireOp",EDGE,"E14.24.MirrorCS")])]})});
            var Q13;
            Q13=makeQuery(id+"F5.boolean.opBoolean","COPY",EDGE,{"derivedFrom":makeQuery(id+"F5.opExtrude","SWEPT_EDGE",EDGE,{"disambiguationData":[OSD([sQuery(id+"F0.wireOp",EDGE,"E0.top"),sQuery(id+"F4.wireOp",EDGE,"E14.8.MirrorCS"),sQuery(id+"F4.wireOp",EDGE,"E14.36.MirrorCS")])]})});
            var Q14;
            Q14=makeQuery(id+"F5.boolean.opBoolean","COPY",EDGE,{"derivedFrom":makeQuery(id+"F5.opExtrude","SWEPT_EDGE",EDGE,{"disambiguationData":[OSD([sQuery(id+"F0.wireOp",EDGE,"E0.top"),sQuery(id+"F4.wireOp",EDGE,"E14.1.MirrorCS"),sQuery(id+"F4.wireOp",EDGE,"E14.21.MirrorCS")])]})});
            var Q15;
            Q15=makeQuery(id+"F5.boolean.opBoolean","COPY",EDGE,{"derivedFrom":makeQuery(id+"F5.opExtrude","SWEPT_EDGE",EDGE,{"disambiguationData":[OSD([sQuery(id+"F0.wireOp",EDGE,"E0.top"),sQuery(id+"F4.wireOp",EDGE,"E14.1.MirrorCS"),sQuery(id+"F4.wireOp",EDGE,"E14.18.MirrorCS")])]})});
            var Q16;
            Q16=makeQuery(id+"F5.boolean.opBoolean","COPY",EDGE,{"derivedFrom":makeQuery(id+"F5.opExtrude","SWEPT_EDGE",EDGE,{"disambiguationData":[OSD([sQuery(id+"F0.wireOp",EDGE,"E0.top"),sQuery(id+"F4.wireOp",EDGE,"E14.10.MirrorCS"),sQuery(id+"F4.wireOp",EDGE,"E14.42.MirrorCS")])]})});
            var Q17;
            Q17=makeQuery(id+"F5.boolean.opBoolean","COPY",EDGE,{"derivedFrom":makeQuery(id+"F5.opExtrude","SWEPT_EDGE",EDGE,{"disambiguationData":[OSD([sQuery(id+"F0.wireOp",EDGE,"E0.top"),sQuery(id+"F4.wireOp",EDGE,"E14.10.MirrorCS"),sQuery(id+"F4.wireOp",EDGE,"E14.48.MirrorCS")])]})});
            var Q18;
            Q18=makeQuery(id+"F5.boolean.opBoolean","COPY",EDGE,{"derivedFrom":makeQuery(id+"F5.opExtrude","SWEPT_EDGE",EDGE,{"disambiguationData":[OSD([sQuery(id+"F0.wireOp",EDGE,"E0.top"),sQuery(id+"F4.wireOp",EDGE,"E14.9.MirrorCS"),sQuery(id+"F4.wireOp",EDGE,"E14.26.MirrorCS")])]})});
            var Q19;
            Q19=makeQuery(id+"F5.boolean.opBoolean","COPY",EDGE,{"derivedFrom":makeQuery(id+"F5.opExtrude","SWEPT_EDGE",EDGE,{"disambiguationData":[OSD([sQuery(id+"F0.wireOp",EDGE,"E0.top"),sQuery(id+"F4.wireOp",EDGE,"E14.9.MirrorCS"),sQuery(id+"F4.wireOp",EDGE,"E14.39.MirrorCS")])]})});
            var Q20;
            Q20=makeQuery(id+"F5.boolean.opBoolean","COPY",EDGE,{"derivedFrom":makeQuery(id+"F5.opExtrude","SWEPT_EDGE",EDGE,{"disambiguationData":[OSD([sQuery(id+"F0.wireOp",EDGE,"E0.top"),sQuery(id+"F4.wireOp",EDGE,"E14.14.MirrorCS"),sQuery(id+"F4.wireOp",EDGE,"E14.22.MirrorCS")])]})});
            var Q21;
            Q21=makeQuery(id+"F5.boolean.opBoolean","COPY",EDGE,{"derivedFrom":makeQuery(id+"F5.opExtrude","SWEPT_EDGE",EDGE,{"disambiguationData":[OSD([sQuery(id+"F0.wireOp",EDGE,"E0.top"),sQuery(id+"F4.wireOp",EDGE,"E14.14.MirrorCS"),sQuery(id+"F4.wireOp",EDGE,"E14.19.MirrorCS")])]})});
            var Q22;
            Q22=makeQuery(id+"F5.boolean.opBoolean","COPY",EDGE,{"derivedFrom":makeQuery(id+"F5.opExtrude","SWEPT_EDGE",EDGE,{"disambiguationData":[OSD([sQuery(id+"F0.wireOp",EDGE,"E0.top"),sQuery(id+"F4.wireOp",EDGE,"E14.6.MirrorCS"),sQuery(id+"F4.wireOp",EDGE,"E14.37.MirrorCS")])]})});
            var Q23;
            Q23=makeQuery(id+"F5.boolean.opBoolean","COPY",EDGE,{"derivedFrom":makeQuery(id+"F5.opExtrude","SWEPT_EDGE",EDGE,{"disambiguationData":[OSD([sQuery(id+"F0.wireOp",EDGE,"E0.top"),sQuery(id+"F4.wireOp",EDGE,"E14.6.MirrorCS"),sQuery(id+"F4.wireOp",EDGE,"E14.34.MirrorCS")])]})});
            var Q24;
            Q24=makeQuery(id+"F5.boolean.opBoolean","COPY",EDGE,{"derivedFrom":makeQuery(id+"F5.opExtrude","SWEPT_EDGE",EDGE,{"disambiguationData":[OSD([sQuery(id+"F0.wireOp",EDGE,"E0.top"),sQuery(id+"F4.wireOp",EDGE,"E14.5.MirrorCS"),sQuery(id+"F4.wireOp",EDGE,"E14.17.MirrorCS")])]})});
            var Q25;
            Q25=makeQuery(id+"F5.boolean.opBoolean","COPY",EDGE,{"derivedFrom":makeQuery(id+"F5.opExtrude","SWEPT_EDGE",EDGE,{"disambiguationData":[OSD([sQuery(id+"F0.wireOp",EDGE,"E0.top"),sQuery(id+"F4.wireOp",EDGE,"E14.5.MirrorCS"),sQuery(id+"F4.wireOp",EDGE,"E14.28.MirrorCS")])]})});
            var Q26;
            Q26=makeQuery(id+"F5.boolean.opBoolean","COPY",EDGE,{"derivedFrom":makeQuery(id+"F5.opExtrude","SWEPT_EDGE",EDGE,{"disambiguationData":[OSD([sQuery(id+"F0.wireOp",EDGE,"E0.top"),sQuery(id+"F4.wireOp",EDGE,"E14.15.MirrorCS"),sQuery(id+"F4.wireOp",EDGE,"E14.46.MirrorCS")])]})});
            var Q27;
            Q27=makeQuery(id+"F5.boolean.opBoolean","COPY",EDGE,{"derivedFrom":makeQuery(id+"F5.opExtrude","SWEPT_EDGE",EDGE,{"disambiguationData":[OSD([sQuery(id+"F0.wireOp",EDGE,"E0.top"),sQuery(id+"F4.wireOp",EDGE,"E14.15.MirrorCS"),sQuery(id+"F4.wireOp",EDGE,"E14.44.MirrorCS")])]})});
            var Q28;
            Q28=makeQuery(id+"F5.boolean.opBoolean","COPY",EDGE,{"derivedFrom":makeQuery(id+"F5.opExtrude","SWEPT_EDGE",EDGE,{"disambiguationData":[OSD([sQuery(id+"F0.wireOp",EDGE,"E0.bottom"),sQuery(id+"F4.wireOp",EDGE,"E5"),sQuery(id+"F4.wireOp",EDGE,"E7")])]})});
            var Q29;
            Q29=makeQuery(id+"F5.boolean.opBoolean","COPY",EDGE,{"derivedFrom":makeQuery(id+"F5.opExtrude","SWEPT_EDGE",EDGE,{"disambiguationData":[OSD([sQuery(id+"F0.wireOp",EDGE,"E0.bottom"),sQuery(id+"F4.wireOp",EDGE,"E13.1.0.1"),sQuery(id+"F4.wireOp",EDGE,"E13.1.0.2")])]})});
            var Q30;
            Q30=makeQuery(id+"F5.boolean.opBoolean","COPY",EDGE,{"derivedFrom":makeQuery(id+"F5.opExtrude","SWEPT_EDGE",EDGE,{"disambiguationData":[OSD([sQuery(id+"F0.wireOp",EDGE,"E0.bottom"),sQuery(id+"F4.wireOp",EDGE,"E13.2.0.1"),sQuery(id+"F4.wireOp",EDGE,"E13.2.0.2")])]})});
            var Q31;
            Q31=makeQuery(id+"F5.boolean.opBoolean","COPY",EDGE,{"derivedFrom":makeQuery(id+"F5.opExtrude","SWEPT_EDGE",EDGE,{"disambiguationData":[OSD([sQuery(id+"F0.wireOp",EDGE,"E0.bottom"),sQuery(id+"F4.wireOp",EDGE,"E13.3.0.1"),sQuery(id+"F4.wireOp",EDGE,"E13.3.0.2")])]})});
            var Q32;
            Q32=makeQuery(id+"F5.boolean.opBoolean","COPY",EDGE,{"derivedFrom":makeQuery(id+"F5.opExtrude","SWEPT_EDGE",EDGE,{"disambiguationData":[OSD([sQuery(id+"F0.wireOp",EDGE,"E0.bottom"),sQuery(id+"F4.wireOp",EDGE,"E13.4.0.1"),sQuery(id+"F4.wireOp",EDGE,"E13.4.0.2")])]})});
            var Q33;
            Q33=makeQuery(id+"F5.boolean.opBoolean","COPY",EDGE,{"derivedFrom":makeQuery(id+"F5.opExtrude","SWEPT_EDGE",EDGE,{"disambiguationData":[OSD([sQuery(id+"F0.wireOp",EDGE,"E0.bottom"),sQuery(id+"F4.wireOp",EDGE,"E13.5.0.1"),sQuery(id+"F4.wireOp",EDGE,"E13.5.0.2")])]})});
            var Q34;
            Q34=makeQuery(id+"F5.boolean.opBoolean","COPY",EDGE,{"derivedFrom":makeQuery(id+"F5.opExtrude","SWEPT_EDGE",EDGE,{"disambiguationData":[OSD([sQuery(id+"F0.wireOp",EDGE,"E0.bottom"),sQuery(id+"F4.wireOp",EDGE,"E13.6.0.1"),sQuery(id+"F4.wireOp",EDGE,"E13.6.0.2")])]})});
            var Q35;
            Q35=makeQuery(id+"F5.boolean.opBoolean","COPY",EDGE,{"derivedFrom":makeQuery(id+"F5.opExtrude","SWEPT_EDGE",EDGE,{"disambiguationData":[OSD([sQuery(id+"F0.wireOp",EDGE,"E0.bottom"),sQuery(id+"F4.wireOp",EDGE,"E13.7.0.1"),sQuery(id+"F4.wireOp",EDGE,"E13.7.0.2")])]})});
            var Q36;
            Q36=makeQuery(id+"F5.boolean.opBoolean","COPY",EDGE,{"derivedFrom":makeQuery(id+"F5.opExtrude","SWEPT_EDGE",EDGE,{"disambiguationData":[OSD([sQuery(id+"F0.wireOp",EDGE,"E0.bottom"),sQuery(id+"F4.wireOp",EDGE,"E13.13.0.1"),sQuery(id+"F4.wireOp",EDGE,"E13.13.0.2")])]})});
            var Q37;
            Q37=makeQuery(id+"F5.boolean.opBoolean","COPY",EDGE,{"derivedFrom":makeQuery(id+"F5.opExtrude","SWEPT_EDGE",EDGE,{"disambiguationData":[OSD([sQuery(id+"F0.wireOp",EDGE,"E0.bottom"),sQuery(id+"F4.wireOp",EDGE,"E13.12.0.1"),sQuery(id+"F4.wireOp",EDGE,"E13.12.0.2")])]})});
            var Q38;
            Q38=makeQuery(id+"F5.boolean.opBoolean","COPY",EDGE,{"derivedFrom":makeQuery(id+"F5.opExtrude","SWEPT_EDGE",EDGE,{"disambiguationData":[OSD([sQuery(id+"F0.wireOp",EDGE,"E0.bottom"),sQuery(id+"F4.wireOp",EDGE,"E13.11.0.1"),sQuery(id+"F4.wireOp",EDGE,"E13.11.0.2")])]})});
            var Q39;
            Q39=makeQuery(id+"F5.boolean.opBoolean","COPY",EDGE,{"derivedFrom":makeQuery(id+"F5.opExtrude","SWEPT_EDGE",EDGE,{"disambiguationData":[OSD([sQuery(id+"F0.wireOp",EDGE,"E0.bottom"),sQuery(id+"F4.wireOp",EDGE,"E13.10.0.1"),sQuery(id+"F4.wireOp",EDGE,"E13.10.0.2")])]})});
            var Q40;
            Q40=makeQuery(id+"F5.boolean.opBoolean","COPY",EDGE,{"derivedFrom":makeQuery(id+"F5.opExtrude","SWEPT_EDGE",EDGE,{"disambiguationData":[OSD([sQuery(id+"F0.wireOp",EDGE,"E0.bottom"),sQuery(id+"F4.wireOp",EDGE,"E13.9.0.1"),sQuery(id+"F4.wireOp",EDGE,"E13.9.0.2")])]})});
            var Q41;
            Q41=makeQuery(id+"F5.boolean.opBoolean","COPY",EDGE,{"derivedFrom":makeQuery(id+"F5.opExtrude","SWEPT_EDGE",EDGE,{"disambiguationData":[OSD([sQuery(id+"F0.wireOp",EDGE,"E0.bottom"),sQuery(id+"F4.wireOp",EDGE,"E13.8.0.1"),sQuery(id+"F4.wireOp",EDGE,"E13.8.0.2")])]})});
            var Q42;
            Q42=makeQuery(id+"F5.boolean.opBoolean","COPY",EDGE,{"derivedFrom":makeQuery(id+"F5.opExtrude","SWEPT_EDGE",EDGE,{"disambiguationData":[OSD([sQuery(id+"F0.wireOp",EDGE,"E0.bottom"),sQuery(id+"F4.wireOp",EDGE,"E13.13.0.0"),sQuery(id+"F4.wireOp",EDGE,"E13.13.0.2")])]})});
            var Q43;
            Q43=makeQuery(id+"F5.boolean.opBoolean","COPY",EDGE,{"derivedFrom":makeQuery(id+"F5.opExtrude","SWEPT_EDGE",EDGE,{"disambiguationData":[OSD([sQuery(id+"F0.wireOp",EDGE,"E0.bottom"),sQuery(id+"F4.wireOp",EDGE,"E13.12.0.0"),sQuery(id+"F4.wireOp",EDGE,"E13.12.0.2")])]})});
            var Q44;
            Q44=makeQuery(id+"F5.boolean.opBoolean","COPY",EDGE,{"derivedFrom":makeQuery(id+"F5.opExtrude","SWEPT_EDGE",EDGE,{"disambiguationData":[OSD([sQuery(id+"F0.wireOp",EDGE,"E0.bottom"),sQuery(id+"F4.wireOp",EDGE,"E13.11.0.0"),sQuery(id+"F4.wireOp",EDGE,"E13.11.0.2")])]})});
            var Q45;
            Q45=makeQuery(id+"F5.boolean.opBoolean","COPY",EDGE,{"derivedFrom":makeQuery(id+"F5.opExtrude","SWEPT_EDGE",EDGE,{"disambiguationData":[OSD([sQuery(id+"F0.wireOp",EDGE,"E0.bottom"),sQuery(id+"F4.wireOp",EDGE,"E13.10.0.0"),sQuery(id+"F4.wireOp",EDGE,"E13.10.0.2")])]})});
            var Q46;
            Q46=makeQuery(id+"F5.boolean.opBoolean","COPY",EDGE,{"derivedFrom":makeQuery(id+"F5.opExtrude","SWEPT_EDGE",EDGE,{"disambiguationData":[OSD([sQuery(id+"F0.wireOp",EDGE,"E0.bottom"),sQuery(id+"F4.wireOp",EDGE,"E13.9.0.0"),sQuery(id+"F4.wireOp",EDGE,"E13.9.0.2")])]})});
            var Q47;
            Q47=makeQuery(id+"F5.boolean.opBoolean","COPY",EDGE,{"derivedFrom":makeQuery(id+"F5.opExtrude","SWEPT_EDGE",EDGE,{"disambiguationData":[OSD([sQuery(id+"F0.wireOp",EDGE,"E0.bottom"),sQuery(id+"F4.wireOp",EDGE,"E13.8.0.0"),sQuery(id+"F4.wireOp",EDGE,"E13.8.0.2")])]})});
            var Q48;
            Q48=makeQuery(id+"F5.boolean.opBoolean","COPY",EDGE,{"derivedFrom":makeQuery(id+"F5.opExtrude","SWEPT_EDGE",EDGE,{"disambiguationData":[OSD([sQuery(id+"F0.wireOp",EDGE,"E0.bottom"),sQuery(id+"F4.wireOp",EDGE,"E13.6.0.0"),sQuery(id+"F4.wireOp",EDGE,"E13.6.0.2")])]})});
            var Q49;
            Q49=makeQuery(id+"F5.boolean.opBoolean","COPY",EDGE,{"derivedFrom":makeQuery(id+"F5.opExtrude","SWEPT_EDGE",EDGE,{"disambiguationData":[OSD([sQuery(id+"F0.wireOp",EDGE,"E0.bottom"),sQuery(id+"F4.wireOp",EDGE,"E13.5.0.0"),sQuery(id+"F4.wireOp",EDGE,"E13.5.0.2")])]})});
            var Q50;
            Q50=makeQuery(id+"F5.boolean.opBoolean","COPY",EDGE,{"derivedFrom":makeQuery(id+"F5.opExtrude","SWEPT_EDGE",EDGE,{"disambiguationData":[OSD([sQuery(id+"F0.wireOp",EDGE,"E0.bottom"),sQuery(id+"F4.wireOp",EDGE,"E13.4.0.0"),sQuery(id+"F4.wireOp",EDGE,"E13.4.0.2")])]})});
            var Q51;
            Q51=makeQuery(id+"F5.boolean.opBoolean","COPY",EDGE,{"derivedFrom":makeQuery(id+"F5.opExtrude","SWEPT_EDGE",EDGE,{"disambiguationData":[OSD([sQuery(id+"F0.wireOp",EDGE,"E0.bottom"),sQuery(id+"F4.wireOp",EDGE,"E13.3.0.0"),sQuery(id+"F4.wireOp",EDGE,"E13.3.0.2")])]})});
            var Q52;
            Q52=makeQuery(id+"F5.boolean.opBoolean","COPY",EDGE,{"derivedFrom":makeQuery(id+"F5.opExtrude","SWEPT_EDGE",EDGE,{"disambiguationData":[OSD([sQuery(id+"F0.wireOp",EDGE,"E0.bottom"),sQuery(id+"F4.wireOp",EDGE,"E13.1.0.0"),sQuery(id+"F4.wireOp",EDGE,"E13.1.0.2")])]})});
            var Q53;
            Q53=makeQuery(id+"F5.boolean.opBoolean","COPY",EDGE,{"derivedFrom":makeQuery(id+"F5.opExtrude","SWEPT_EDGE",EDGE,{"disambiguationData":[OSD([sQuery(id+"F0.wireOp",EDGE,"E0.bottom"),sQuery(id+"F4.wireOp",EDGE,"E6"),sQuery(id+"F4.wireOp",EDGE,"E7")])]})});
            var Q54;
            Q54=makeQuery(id+"F5.boolean.opBoolean","COPY",EDGE,{"derivedFrom":makeQuery(id+"F5.opExtrude","SWEPT_EDGE",EDGE,{"disambiguationData":[OSD([sQuery(id+"F0.wireOp",EDGE,"E0.bottom"),sQuery(id+"F4.wireOp",EDGE,"E13.2.0.0"),sQuery(id+"F4.wireOp",EDGE,"E13.2.0.2")])]})});
            var Q55;
            Q55=makeQuery(id+"F5.boolean.opBoolean","COPY",EDGE,{"derivedFrom":makeQuery(id+"F5.opExtrude","SWEPT_EDGE",EDGE,{"disambiguationData":[OSD([sQuery(id+"F0.wireOp",EDGE,"E0.bottom"),sQuery(id+"F4.wireOp",EDGE,"E13.7.0.0"),sQuery(id+"F4.wireOp",EDGE,"E13.7.0.2")])]})});
            fillet(context, id + "F7", {"entities" : qUnion([Q0, Q1, Q2, Q3, Q4, Q5, Q6, Q7, Q8, Q9, Q10, Q11, Q12, Q13, Q14, Q15, Q16, Q17, Q18, Q19, Q20, Q21, Q22, Q23, Q24, Q25, Q26, Q27, Q28, Q29, Q30, Q31, Q32, Q33, Q34, Q35, Q36, Q37, Q38, Q39, Q40, Q41, Q42, Q43, Q44, Q45, Q46, Q47, Q48, Q49, Q50, Q51, Q52, Q53, Q54, Q55]), "radius" : 1.27 * mm, "tangentPropagation" : true, "allowEdgeOverflow" : false});
        }
        {
            var Q0;
            Q0=makeQuery(id+"F5.boolean.opBoolean","COPY",EDGE,{"derivedFrom":makeQuery(id+"F5.opExtrude","SWEPT_EDGE",EDGE,{"disambiguationData":[OSD([sQuery(id+"F4.wireOp",EDGE,"E18"),sQuery(id+"F4.wireOp",EDGE,"E20")])]})});
            var Q1;
            Q1=makeQuery(id+"F5.boolean.opBoolean","COPY",EDGE,{"derivedFrom":makeQuery(id+"F5.opExtrude","SWEPT_EDGE",EDGE,{"disambiguationData":[OSD([sQuery(id+"F4.wireOp",EDGE,"E21.1.0.2"),sQuery(id+"F4.wireOp",EDGE,"E21.1.0.3")])]})});
            var Q2;
            Q2=makeQuery(id+"F5.boolean.opBoolean","COPY",EDGE,{"derivedFrom":makeQuery(id+"F5.opExtrude","SWEPT_EDGE",EDGE,{"disambiguationData":[OSD([sQuery(id+"F4.wireOp",EDGE,"E21.2.0.2"),sQuery(id+"F4.wireOp",EDGE,"E21.2.0.3")])]})});
            var Q3;
            Q3=makeQuery(id+"F5.boolean.opBoolean","COPY",EDGE,{"derivedFrom":makeQuery(id+"F5.opExtrude","SWEPT_EDGE",EDGE,{"disambiguationData":[OSD([sQuery(id+"F4.wireOp",EDGE,"E21.3.0.2"),sQuery(id+"F4.wireOp",EDGE,"E21.3.0.3")])]})});
            var Q4;
            Q4=makeQuery(id+"F5.boolean.opBoolean","COPY",EDGE,{"derivedFrom":makeQuery(id+"F5.opExtrude","SWEPT_EDGE",EDGE,{"disambiguationData":[OSD([sQuery(id+"F4.wireOp",EDGE,"E21.4.0.2"),sQuery(id+"F4.wireOp",EDGE,"E21.4.0.3")])]})});
            var Q5;
            Q5=makeQuery(id+"F5.boolean.opBoolean","COPY",EDGE,{"derivedFrom":makeQuery(id+"F5.opExtrude","SWEPT_EDGE",EDGE,{"disambiguationData":[OSD([sQuery(id+"F4.wireOp",EDGE,"E21.5.0.2"),sQuery(id+"F4.wireOp",EDGE,"E21.5.0.3")])]})});
            var Q6;
            Q6=makeQuery(id+"F5.boolean.opBoolean","COPY",EDGE,{"derivedFrom":makeQuery(id+"F5.opExtrude","SWEPT_EDGE",EDGE,{"disambiguationData":[OSD([sQuery(id+"F4.wireOp",EDGE,"E21.6.0.2"),sQuery(id+"F4.wireOp",EDGE,"E21.6.0.3")])]})});
            var Q7;
            Q7=makeQuery(id+"F5.boolean.opBoolean","COPY",EDGE,{"derivedFrom":makeQuery(id+"F5.opExtrude","SWEPT_EDGE",EDGE,{"disambiguationData":[OSD([sQuery(id+"F4.wireOp",EDGE,"E21.7.0.2"),sQuery(id+"F4.wireOp",EDGE,"E21.7.0.3")])]})});
            var Q8;
            Q8=makeQuery(id+"F5.boolean.opBoolean","COPY",EDGE,{"derivedFrom":makeQuery(id+"F5.opExtrude","SWEPT_EDGE",EDGE,{"disambiguationData":[OSD([sQuery(id+"F4.wireOp",EDGE,"E21.8.0.2"),sQuery(id+"F4.wireOp",EDGE,"E21.8.0.3")])]})});
            var Q9;
            Q9=makeQuery(id+"F5.boolean.opBoolean","COPY",EDGE,{"derivedFrom":makeQuery(id+"F5.opExtrude","SWEPT_EDGE",EDGE,{"disambiguationData":[OSD([sQuery(id+"F4.wireOp",EDGE,"E21.9.0.2"),sQuery(id+"F4.wireOp",EDGE,"E21.9.0.3")])]})});
            var Q10;
            Q10=makeQuery(id+"F5.boolean.opBoolean","COPY",EDGE,{"derivedFrom":makeQuery(id+"F5.opExtrude","SWEPT_EDGE",EDGE,{"disambiguationData":[OSD([sQuery(id+"F4.wireOp",EDGE,"E21.10.0.2"),sQuery(id+"F4.wireOp",EDGE,"E21.10.0.3")])]})});
            var Q11;
            Q11=makeQuery(id+"F5.boolean.opBoolean","COPY",EDGE,{"derivedFrom":makeQuery(id+"F5.opExtrude","SWEPT_EDGE",EDGE,{"disambiguationData":[OSD([sQuery(id+"F4.wireOp",EDGE,"E21.11.0.2"),sQuery(id+"F4.wireOp",EDGE,"E21.11.0.3")])]})});
            var Q12;
            Q12=makeQuery(id+"F5.boolean.opBoolean","COPY",EDGE,{"derivedFrom":makeQuery(id+"F5.opExtrude","SWEPT_EDGE",EDGE,{"disambiguationData":[OSD([sQuery(id+"F4.wireOp",EDGE,"E21.13.0.2"),sQuery(id+"F4.wireOp",EDGE,"E21.13.0.3")])]})});
            var Q13;
            Q13=makeQuery(id+"F5.boolean.opBoolean","COPY",EDGE,{"derivedFrom":makeQuery(id+"F5.opExtrude","SWEPT_EDGE",EDGE,{"disambiguationData":[OSD([sQuery(id+"F4.wireOp",EDGE,"E21.12.0.2"),sQuery(id+"F4.wireOp",EDGE,"E21.12.0.3")])]})});
            var Q14;
            Q14=makeQuery(id+"F5.boolean.opBoolean","COPY",EDGE,{"derivedFrom":makeQuery(id+"F5.opExtrude","SWEPT_EDGE",EDGE,{"disambiguationData":[OSD([sQuery(id+"F4.wireOp",EDGE,"E21.13.0.0"),sQuery(id+"F4.wireOp",EDGE,"E21.13.0.1")])]})});
            var Q15;
            Q15=makeQuery(id+"F5.boolean.opBoolean","COPY",EDGE,{"derivedFrom":makeQuery(id+"F5.opExtrude","SWEPT_EDGE",EDGE,{"disambiguationData":[OSD([sQuery(id+"F4.wireOp",EDGE,"E21.12.0.0"),sQuery(id+"F4.wireOp",EDGE,"E21.12.0.1")])]})});
            var Q16;
            Q16=makeQuery(id+"F5.boolean.opBoolean","COPY",EDGE,{"derivedFrom":makeQuery(id+"F5.opExtrude","SWEPT_EDGE",EDGE,{"disambiguationData":[OSD([sQuery(id+"F4.wireOp",EDGE,"E21.11.0.0"),sQuery(id+"F4.wireOp",EDGE,"E21.11.0.1")])]})});
            var Q17;
            Q17=makeQuery(id+"F5.boolean.opBoolean","COPY",EDGE,{"derivedFrom":makeQuery(id+"F5.opExtrude","SWEPT_EDGE",EDGE,{"disambiguationData":[OSD([sQuery(id+"F4.wireOp",EDGE,"E21.10.0.0"),sQuery(id+"F4.wireOp",EDGE,"E21.10.0.1")])]})});
            var Q18;
            Q18=makeQuery(id+"F5.boolean.opBoolean","COPY",EDGE,{"derivedFrom":makeQuery(id+"F5.opExtrude","SWEPT_EDGE",EDGE,{"disambiguationData":[OSD([sQuery(id+"F4.wireOp",EDGE,"E21.9.0.0"),sQuery(id+"F4.wireOp",EDGE,"E21.9.0.1")])]})});
            var Q19;
            Q19=makeQuery(id+"F5.boolean.opBoolean","COPY",EDGE,{"derivedFrom":makeQuery(id+"F5.opExtrude","SWEPT_EDGE",EDGE,{"disambiguationData":[OSD([sQuery(id+"F4.wireOp",EDGE,"E21.8.0.0"),sQuery(id+"F4.wireOp",EDGE,"E21.8.0.1")])]})});
            var Q20;
            Q20=makeQuery(id+"F5.boolean.opBoolean","COPY",EDGE,{"derivedFrom":makeQuery(id+"F5.opExtrude","SWEPT_EDGE",EDGE,{"disambiguationData":[OSD([sQuery(id+"F4.wireOp",EDGE,"E21.7.0.0"),sQuery(id+"F4.wireOp",EDGE,"E21.7.0.1")])]})});
            var Q21;
            Q21=makeQuery(id+"F5.boolean.opBoolean","COPY",EDGE,{"derivedFrom":makeQuery(id+"F5.opExtrude","SWEPT_EDGE",EDGE,{"disambiguationData":[OSD([sQuery(id+"F4.wireOp",EDGE,"E21.6.0.0"),sQuery(id+"F4.wireOp",EDGE,"E21.6.0.1")])]})});
            var Q22;
            Q22=makeQuery(id+"F5.boolean.opBoolean","COPY",EDGE,{"derivedFrom":makeQuery(id+"F5.opExtrude","SWEPT_EDGE",EDGE,{"disambiguationData":[OSD([sQuery(id+"F4.wireOp",EDGE,"E21.5.0.0"),sQuery(id+"F4.wireOp",EDGE,"E21.5.0.1")])]})});
            var Q23;
            Q23=makeQuery(id+"F5.boolean.opBoolean","COPY",EDGE,{"derivedFrom":makeQuery(id+"F5.opExtrude","SWEPT_EDGE",EDGE,{"disambiguationData":[OSD([sQuery(id+"F4.wireOp",EDGE,"E21.4.0.0"),sQuery(id+"F4.wireOp",EDGE,"E21.4.0.1")])]})});
            var Q24;
            Q24=makeQuery(id+"F5.boolean.opBoolean","COPY",EDGE,{"derivedFrom":makeQuery(id+"F5.opExtrude","SWEPT_EDGE",EDGE,{"disambiguationData":[OSD([sQuery(id+"F4.wireOp",EDGE,"E21.3.0.0"),sQuery(id+"F4.wireOp",EDGE,"E21.3.0.1")])]})});
            var Q25;
            Q25=makeQuery(id+"F5.boolean.opBoolean","COPY",EDGE,{"derivedFrom":makeQuery(id+"F5.opExtrude","SWEPT_EDGE",EDGE,{"disambiguationData":[OSD([sQuery(id+"F4.wireOp",EDGE,"E21.2.0.0"),sQuery(id+"F4.wireOp",EDGE,"E21.2.0.1")])]})});
            var Q26;
            Q26=makeQuery(id+"F5.boolean.opBoolean","COPY",EDGE,{"derivedFrom":makeQuery(id+"F5.opExtrude","SWEPT_EDGE",EDGE,{"disambiguationData":[OSD([sQuery(id+"F4.wireOp",EDGE,"E21.1.0.0"),sQuery(id+"F4.wireOp",EDGE,"E21.1.0.1")])]})});
            var Q27;
            Q27=makeQuery(id+"F5.boolean.opBoolean","COPY",EDGE,{"derivedFrom":makeQuery(id+"F5.opExtrude","SWEPT_EDGE",EDGE,{"disambiguationData":[OSD([sQuery(id+"F4.wireOp",EDGE,"E17"),sQuery(id+"F4.wireOp",EDGE,"E19")])]})});
            fillet(context, id + "F8", {"entities" : qUnion([Q0, Q1, Q2, Q3, Q4, Q5, Q6, Q7, Q8, Q9, Q10, Q11, Q12, Q13, Q14, Q15, Q16, Q17, Q18, Q19, Q20, Q21, Q22, Q23, Q24, Q25, Q26, Q27]), "radius" : 0.13 * mm, "tangentPropagation" : true, "allowEdgeOverflow" : false});
        }
    });
